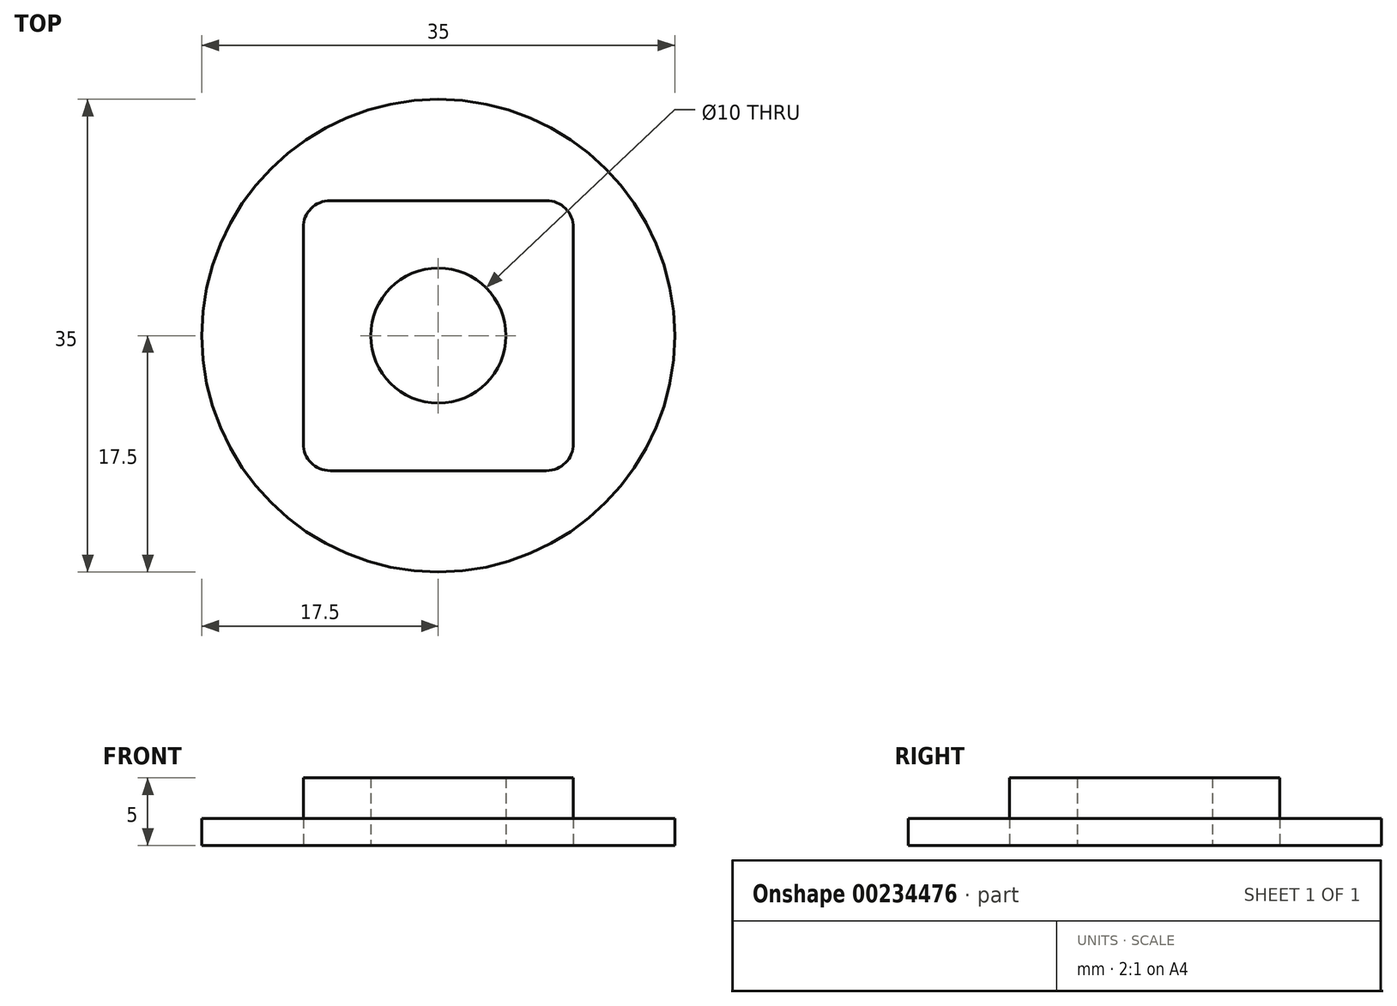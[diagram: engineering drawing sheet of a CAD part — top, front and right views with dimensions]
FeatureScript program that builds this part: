
annotation { "Feature Type Name" : "Feature", "Feature Type Description" : "" }
export const myFeature = defineFeature(function(context is Context, id is Id, definition is map)
    precondition{}
    {
        {
            var Q0;
            Q0=qCreatedBy(makeId("Top.planeOp"),FACE);
            var sketch = newSketch(context, id + "F0", { "sketchPlane" : qUnion([Q0])});
            skCircle(sketch, "E0", {"center": v(0, 0) * mm, "radius": 5 * mm});
            skLineSegment(sketch, "E1.bottom", {"start": v(10, 10) * mm, "end": v(-10, 10) * mm});
            skLineSegment(sketch, "E1.top", {"start": v(10, -10) * mm, "end": v(-10, -10) * mm});
            skLineSegment(sketch, "E1.left", {"start": v(10, 10) * mm, "end": v(10, -10) * mm});
            skLineSegment(sketch, "E1.right", {"start": v(-10, 10) * mm, "end": v(-10, -10) * mm});
            skSolve(sketch);
        }
        {
            var Q0;
            Q0 = qSketchRegion(id + "F0", true);
            extrude(context, id + "F1", {"entities" : qUnion([Q0]), "depth" : 5 * mm, "offsetDistance" : 25 * mm});
        }
        {
            var Q0;
            Q0=makeQuery(id+"F1.opExtrude","SWEPT_EDGE",EDGE,{"disambiguationData":[OSD([sQuery(id+"F0.wireOp",EDGE,"E1.top"),sQuery(id+"F0.wireOp",EDGE,"E1.right")])]});
            var Q1;
            Q1=makeQuery(id+"F1.opExtrude","SWEPT_EDGE",EDGE,{"disambiguationData":[OSD([sQuery(id+"F0.wireOp",EDGE,"E1.top"),sQuery(id+"F0.wireOp",EDGE,"E1.left")])]});
            var Q2;
            Q2=makeQuery(id+"F1.opExtrude","SWEPT_EDGE",EDGE,{"disambiguationData":[OSD([sQuery(id+"F0.wireOp",EDGE,"E1.bottom"),sQuery(id+"F0.wireOp",EDGE,"E1.left")])]});
            var Q3;
            Q3=makeQuery(id+"F1.opExtrude","SWEPT_EDGE",EDGE,{"disambiguationData":[OSD([sQuery(id+"F0.wireOp",EDGE,"E1.bottom"),sQuery(id+"F0.wireOp",EDGE,"E1.right")])]});
            fillet(context, id + "F2", {"entities" : qUnion([Q0, Q1, Q2, Q3]), "tangentPropagation" : true, "radius" : 2 * mm, "defaultsChanged" : false, "vertexSettings" : [], "allowEdgeOverflow" : false});
        }
        {
            var Q0;
            Q0=qCreatedBy(makeId("Top.planeOp"), FACE);
            var sketch = newSketch(context, id + "F3", { "sketchPlane" : qUnion([Q0])});
            skCircle(sketch, "E2", {"center": v(0, 0) * mm, "radius": 17.5 * mm});
            skSolve(sketch);
        }
        {
            var Q0;
            Q0 = qSketchRegion(id + "F3", true);
            extrude(context, id + "F4", {"entities" : qUnion([Q0]), "domain" : OperationDomain.MODEL, "flatOperationType" : FlatOperationType.REMOVE, "depth" : 2 * mm, "offsetDistance" : 25 * mm});
        }
    });
